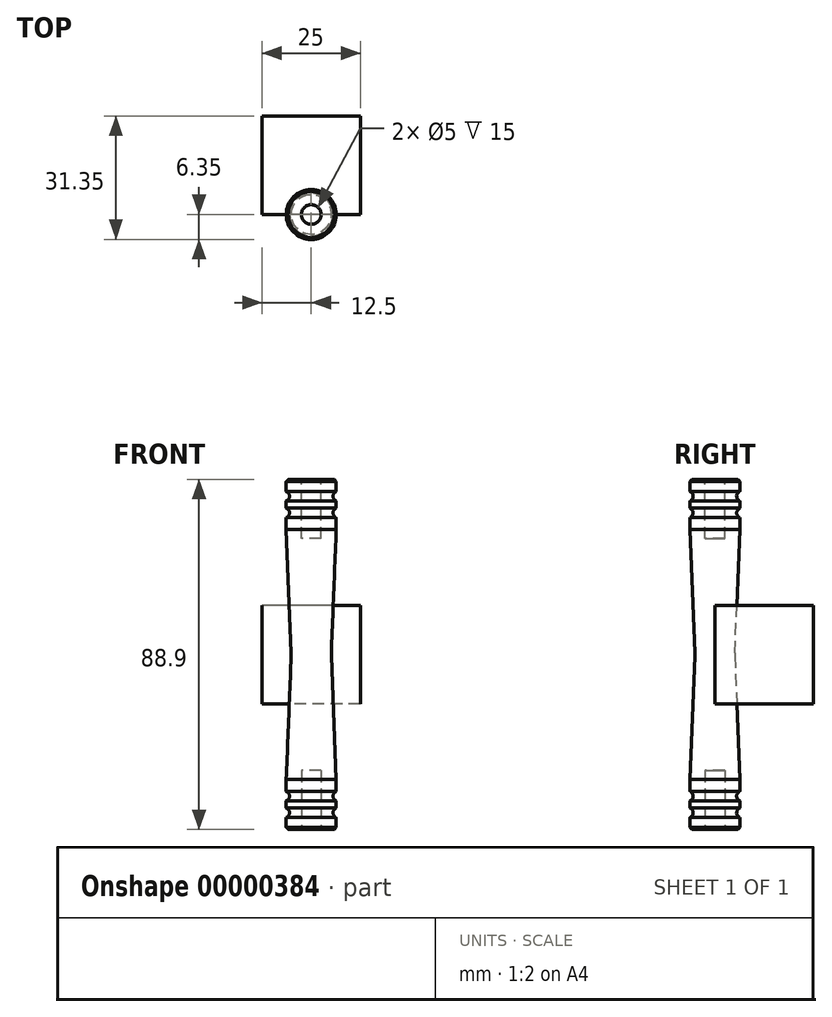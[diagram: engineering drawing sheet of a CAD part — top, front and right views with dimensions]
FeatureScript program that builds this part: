
annotation { "Feature Type Name" : "Feature", "Feature Type Description" : "" }
export const myFeature = defineFeature(function(context is Context, id is Id, definition is map)
    precondition{}
    {
        {
            var Q0;
            Q0=qCreatedBy(makeId("Front.planeOp"),FACE);
            var sketch = newSketch(context, id + "F0", { "sketchPlane" : qUnion([Q0])});
            skLineSegment(sketch, "E0", {"start": v(0, 0) * mm, "end": v(0, 44.45) * mm});
            skLineSegment(sketch, "E1", {"start": v(0, 44.45) * mm, "end": v(6.35, 44.45) * mm});
            skLineSegment(sketch, "E2", {"start": v(6.35, 44.45) * mm, "end": v(6.35, 31.75) * mm});
            skLineSegment(sketch, "E3", {"start": v(0, 0) * mm, "end": v(5.08, 0) * mm});
            skLineSegment(sketch, "E4", {"start": v(6.35, 31.75) * mm, "end": v(5.08, 0) * mm});
            skLineSegment(sketch, "E5", {"start": v(3.18, 44.45) * mm, "end": v(3.18, 40.22) * mm, "construction": true});
            skLineSegment(sketch, "E6", {"start": v(3.18, 40.22) * mm, "end": v(3.18, 35.98) * mm, "construction": true});
            skLineSegment(sketch, "E7", {"start": v(3.18, 35.98) * mm, "end": v(3.18, 31.75) * mm, "construction": true});
            skLineSegment(sketch, "E8", {"start": v(0, 40.22) * mm, "end": v(6.8, 40.22) * mm, "construction": true});
            skLineSegment(sketch, "E9", {"start": v(0, 35.98) * mm, "end": v(6.8, 35.98) * mm, "construction": true});
            skCircle(sketch, "E10", {"center": v(6.8, 40.22) * mm, "radius": 1.27 * mm});
            skCircle(sketch, "E11", {"center": v(6.8, 35.98) * mm, "radius": 1.27 * mm});
            skSolve(sketch);
        }
        {
            var Q0;
            Q0=makeQuery(id+"F0.imprint","IMPRINT",FACE,{"disambiguationData":[TD([[makeQuery(id+"F0.imprint","IMPRINT",EDGE,{"derivedFrom":sQuery(id+"F0.wireOp",EDGE,"E0")}),-1.0]])]});
            var Q1;
            Q1=sQuery(id+"F0.wireOp",EDGE,"E0");
            revolve(context, id + "F1", {"entities" : qUnion([Q0]), "axis" : qUnion([Q1]), "revolveType" : RevolveType.FULL});
        }
        {
            var Q0;
            Q0=makeQuery(id+"F1.opRevolve","SWEPT_EDGE",EDGE,{"disambiguationData":[OSD([sQuery(id+"F0.wireOp",EDGE,"E1"),sQuery(id+"F0.wireOp",EDGE,"E2")])]});
            chamfer(context, id + "F2", {"entities" : qUnion([Q0]), "width" : 0.5 * mm, "tangentPropagation" : true});
        }
        {
            var Q0;
            Q0=makeQuery(id+"F1.opRevolve","SWEPT_FACE",FACE,{"disambiguationData":[OSD([sQuery(id+"F0.wireOp",EDGE,"E1")])]});
            var sketch = newSketch(context, id + "F3", { "sketchPlane" : qUnion([Q0])});
            skCircle(sketch, "E12", {"center": v(0, 0) * mm, "radius": 2.5 * mm});
            skSolve(sketch);
        }
        {
            var Q0;
            Q0=makeQuery(id+"F3.imprint","IMPRINT",FACE,{"disambiguationData":[TD([[makeQuery(id+"F3.imprint","IMPRINT",EDGE,{"derivedFrom":sQuery(id+"F3.wireOp",EDGE,"E12")}),1.0]])]});
            extrude(context, id + "F4", {"entities" : qUnion([Q0]), "operationType" : NewBodyOperationType.REMOVE, "oppositeDirection" : true, "depth" : 15 * mm});
        }
        {
            var Q0;
            Q0=makeQuery(id+"F1.opRevolve","SWEPT_BODY",BODY,{"disambiguationData":[OSD([sQuery(id+"F0.wireOp",EDGE,"E0"),sQuery(id+"F0.wireOp",EDGE,"E1"),sQuery(id+"F0.wireOp",EDGE,"E2"),sQuery(id+"F0.wireOp",EDGE,"E3"),sQuery(id+"F0.wireOp",EDGE,"E4"),sQuery(id+"F0.wireOp",EDGE,"E10"),sQuery(id+"F0.wireOp",EDGE,"E11")])]});
            var Q1;
            Q1=makeQuery(id+"F1.opRevolve","SWEPT_FACE",FACE,{"disambiguationData":[OSD([sQuery(id+"F0.wireOp",EDGE,"E3")])]});
            mirror(context, id + "F5", {"entities" : qUnion([Q0]), "mirrorPlane" : qUnion([Q1])});
        }
        {
            var Q0;
            Q0=makeQuery(id+"F1.opRevolve","SWEPT_BODY",BODY,{"disambiguationData":[OSD([sQuery(id+"F0.wireOp",EDGE,"E0"),sQuery(id+"F0.wireOp",EDGE,"E1"),sQuery(id+"F0.wireOp",EDGE,"E2"),sQuery(id+"F0.wireOp",EDGE,"E3"),sQuery(id+"F0.wireOp",EDGE,"E4"),sQuery(id+"F0.wireOp",EDGE,"E10"),sQuery(id+"F0.wireOp",EDGE,"E11")])]});
            var Q1;
            Q1=makeQuery(id+"F5.opPattern","COPY",BODY,{"derivedFrom":makeQuery(id+"F1.opRevolve","SWEPT_BODY",BODY,{"disambiguationData":[OSD([sQuery(id+"F0.wireOp",EDGE,"E0"),sQuery(id+"F0.wireOp",EDGE,"E1"),sQuery(id+"F0.wireOp",EDGE,"E2"),sQuery(id+"F0.wireOp",EDGE,"E3"),sQuery(id+"F0.wireOp",EDGE,"E4"),sQuery(id+"F0.wireOp",EDGE,"E10"),sQuery(id+"F0.wireOp",EDGE,"E11")])]}),"instanceName":"1"});
            booleanBodies(context, id + "F6", {"operationType" : BooleanOperationType.UNION, "tools" : qUnion([Q0, Q1])});
        }
        {
            var Q0;
            {var subQ0=makeQuery(id+"F1.opRevolve","SWEPT_EDGE",EDGE,{"disambiguationData":[OSD([sQuery(id+"F0.wireOp",EDGE,"E3"),sQuery(id+"F0.wireOp",EDGE,"E4")])]});Q0=makeQuery(id+"F6.opBoolean","MERGE",EDGE,{"derivedFrom":[subQ0,makeQuery(id+"F5.opPattern","COPY",EDGE,{"derivedFrom":subQ0,"instanceName":"1"})]});}
            fillet(context, id + "F7", {"entities" : qUnion([Q0]), "radius" : 10 * mm, "tangentPropagation" : true, "allowEdgeOverflow" : false});
        }
        {
            var Q0;
            Q0=qCreatedBy(makeId("Front.planeOp"),FACE);
            var sketch = newSketch(context, id + "F8", { "sketchPlane" : qUnion([Q0])});
            skLineSegment(sketch, "E13.rect.bottom", {"start": v(12.5, -12.5) * mm, "end": v(-12.5, -12.5) * mm});
            skLineSegment(sketch, "E13.rect.top", {"start": v(12.5, 12.5) * mm, "end": v(-12.5, 12.5) * mm});
            skLineSegment(sketch, "E13.rect.left", {"start": v(12.5, -12.5) * mm, "end": v(12.5, 12.5) * mm});
            skLineSegment(sketch, "E13.rect.right", {"start": v(-12.5, -12.5) * mm, "end": v(-12.5, 12.5) * mm});
            skPoint(sketch, "E13.rect.middle", {"position": v(0, 0) * mm});
            skSolve(sketch);
        }
        {
            var Q0;
            Q0=makeQuery(id+"F8.imprint","IMPRINT",FACE,{"disambiguationData":[TD([[makeQuery(id+"F8.imprint","IMPRINT",EDGE,{"derivedFrom":sQuery(id+"F8.wireOp",EDGE,"E13.rect.bottom")}),-1.0]])]});
            extrude(context, id + "F9", {"entities" : qUnion([Q0]), "oppositeDirection" : true, "depth" : 25 * mm});
        }
    });
